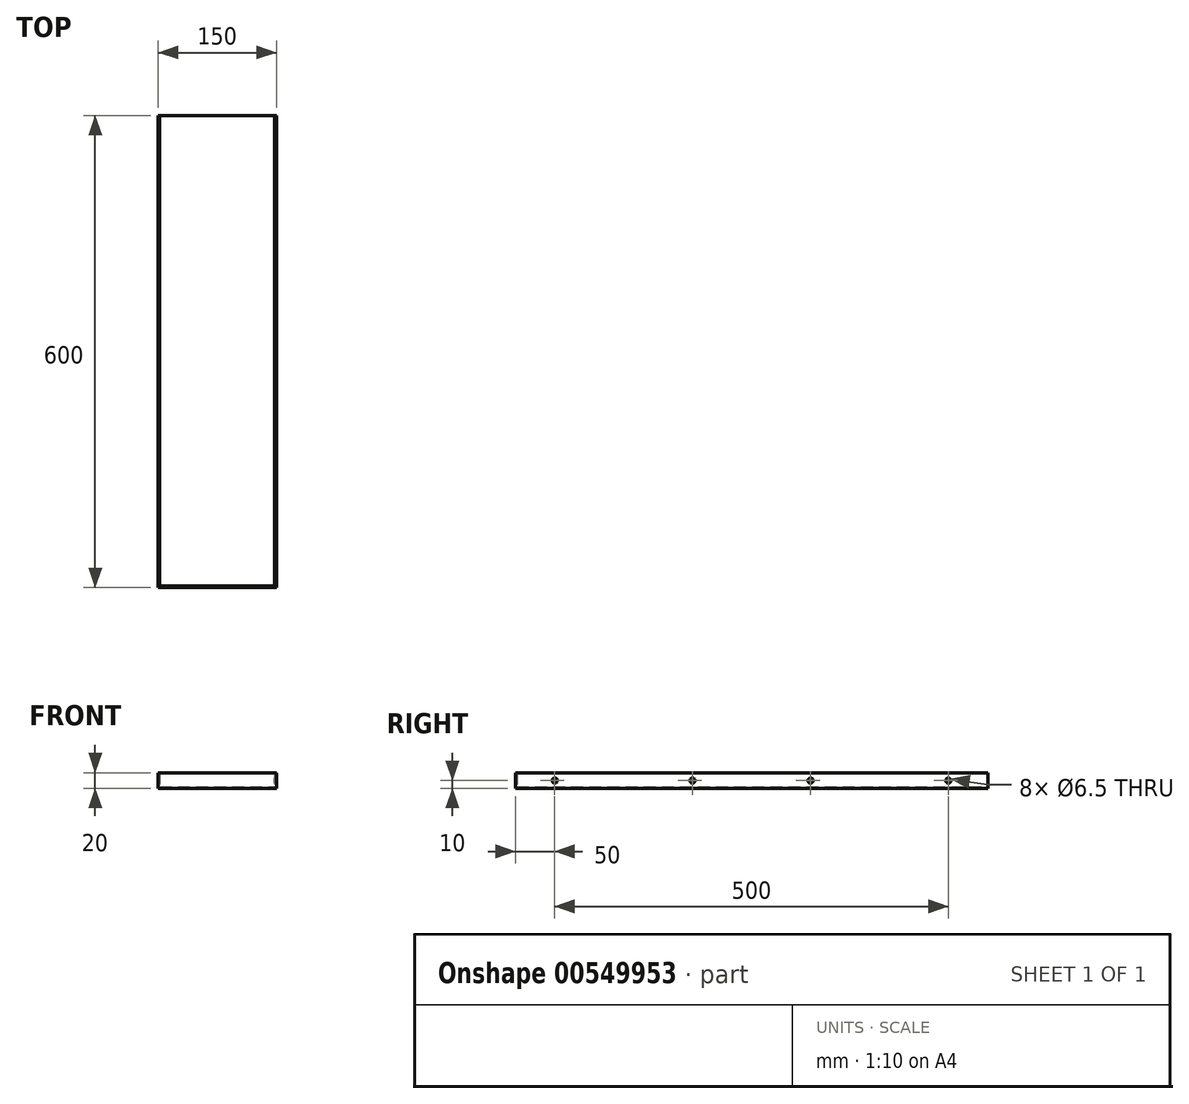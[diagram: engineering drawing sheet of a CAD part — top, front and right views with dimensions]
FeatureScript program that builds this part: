
annotation { "Feature Type Name" : "Feature", "Feature Type Description" : "" }
export const myFeature = defineFeature(function(context is Context, id is Id, definition is map)
    precondition{}
    {
        {
            var Q0;
            Q0=qCreatedBy(makeId("Front.planeOp"),FACE);
            var sketch = newSketch(context, id + "F0", { "sketchPlane" : qUnion([Q0])});
            skLineSegment(sketch, "E0.top", {"start": v(-75, -10) * mm, "end": v(75, -10) * mm});
            skLineSegment(sketch, "E0.left", {"start": v(-75, 10) * mm, "end": v(-75, -10) * mm});
            skLineSegment(sketch, "E0.right", {"start": v(75, 10) * mm, "end": v(75, -10) * mm});
            skPoint(sketch, "E0.middle", {"position": v(0, 0) * mm});
            skLineSegment(sketch, "E1.0", {"start": v(-73, 10) * mm, "end": v(-73, -8) * mm});
            skLineSegment(sketch, "E2.0", {"start": v(73, 10) * mm, "end": v(73, -8) * mm});
            skLineSegment(sketch, "E3.0", {"start": v(-73, -8) * mm, "end": v(73, -8) * mm});
            skLineSegment(sketch, "E4", {"start": v(-73, 10) * mm, "end": v(-75, 10) * mm});
            skLineSegment(sketch, "E5", {"start": v(73, 10) * mm, "end": v(75, 10) * mm});
            skSolve(sketch);
        }
        {
            var Q0;
            Q0=qSketchRegion(id+"F0",true);
            extrude(context, id + "F1", {"entities" : qUnion([Q0]), "depth" : 600 * mm, "offsetDistance" : 25 * mm});
        }
        {
            var Q0;
            Q0=makeQuery(id+"F1.opExtrude","SWEPT_FACE",FACE,{"disambiguationData":[OSD([sQuery(id+"F0.wireOp",EDGE,"E0.left")])]});
            var sketch = newSketch(context, id + "F2", { "sketchPlane" : qUnion([Q0])});
            skCircle(sketch, "E6", {"center": v(225, 0) * mm, "radius": 3.25 * mm});
            skPoint(sketch, "E7", {"position": v(225, 10) * mm});
            skCircle(sketch, "E8", {"center": v(550, 0) * mm, "radius": 3.25 * mm});
            skCircle(sketch, "E9", {"center": v(375, 0) * mm, "radius": 3.25 * mm});
            skCircle(sketch, "E10", {"center": v(50, 0) * mm, "radius": 3.25 * mm});
            skSolve(sketch);
        }
        {
            var Q0;
            Q0 = qSketchRegion(id + "F2", true);
            extrude(context, id + "F3", {"entities" : qUnion([Q0]), "operationType" : NewBodyOperationType.REMOVE, "endBound" : BoundingType.THROUGH_ALL, "oppositeDirection" : true, "depth" : 25 * mm, "offsetDistance" : 25 * mm});
        }
        {
            var Q0;
            Q0=makeQuery(id+"F1.opExtrude","CAP_FACE",FACE,{"disambiguationData":[OSD([sQuery(id+"F0.wireOp",EDGE,"E0.top"),sQuery(id+"F0.wireOp",EDGE,"E0.left"),sQuery(id+"F0.wireOp",EDGE,"E0.right"),sQuery(id+"F0.wireOp",EDGE,"E1.0"),sQuery(id+"F0.wireOp",EDGE,"E2.0"),sQuery(id+"F0.wireOp",EDGE,"E3.0"),sQuery(id+"F0.wireOp",EDGE,"E4"),sQuery(id+"F0.wireOp",EDGE,"E5")])],"isStart":false});
            var sketch = newSketch(context, id + "F4", { "sketchPlane" : qUnion([Q0])});
            skLineSegment(sketch, "E11.0", {"start": v(-75, 10) * mm, "end": v(-75, -10) * mm});
            skLineSegment(sketch, "E12.0", {"start": v(-75, -10) * mm, "end": v(75, -10) * mm});
            skLineSegment(sketch, "E13.0", {"start": v(75, 10) * mm, "end": v(75, -10) * mm});
            skLineSegment(sketch, "E14", {"start": v(75, 10) * mm, "end": v(-75, 10) * mm});
            skSolve(sketch);
        }
        {
            var Q0;
            Q0 = qSketchRegion(id + "F4", true);
            extrude(context, id + "F5", {"entities" : qUnion([Q0]), "operationType" : NewBodyOperationType.ADD, "oppositeDirection" : true, "depth" : 2 * mm, "offsetDistance" : 25 * mm});
        }
    });
